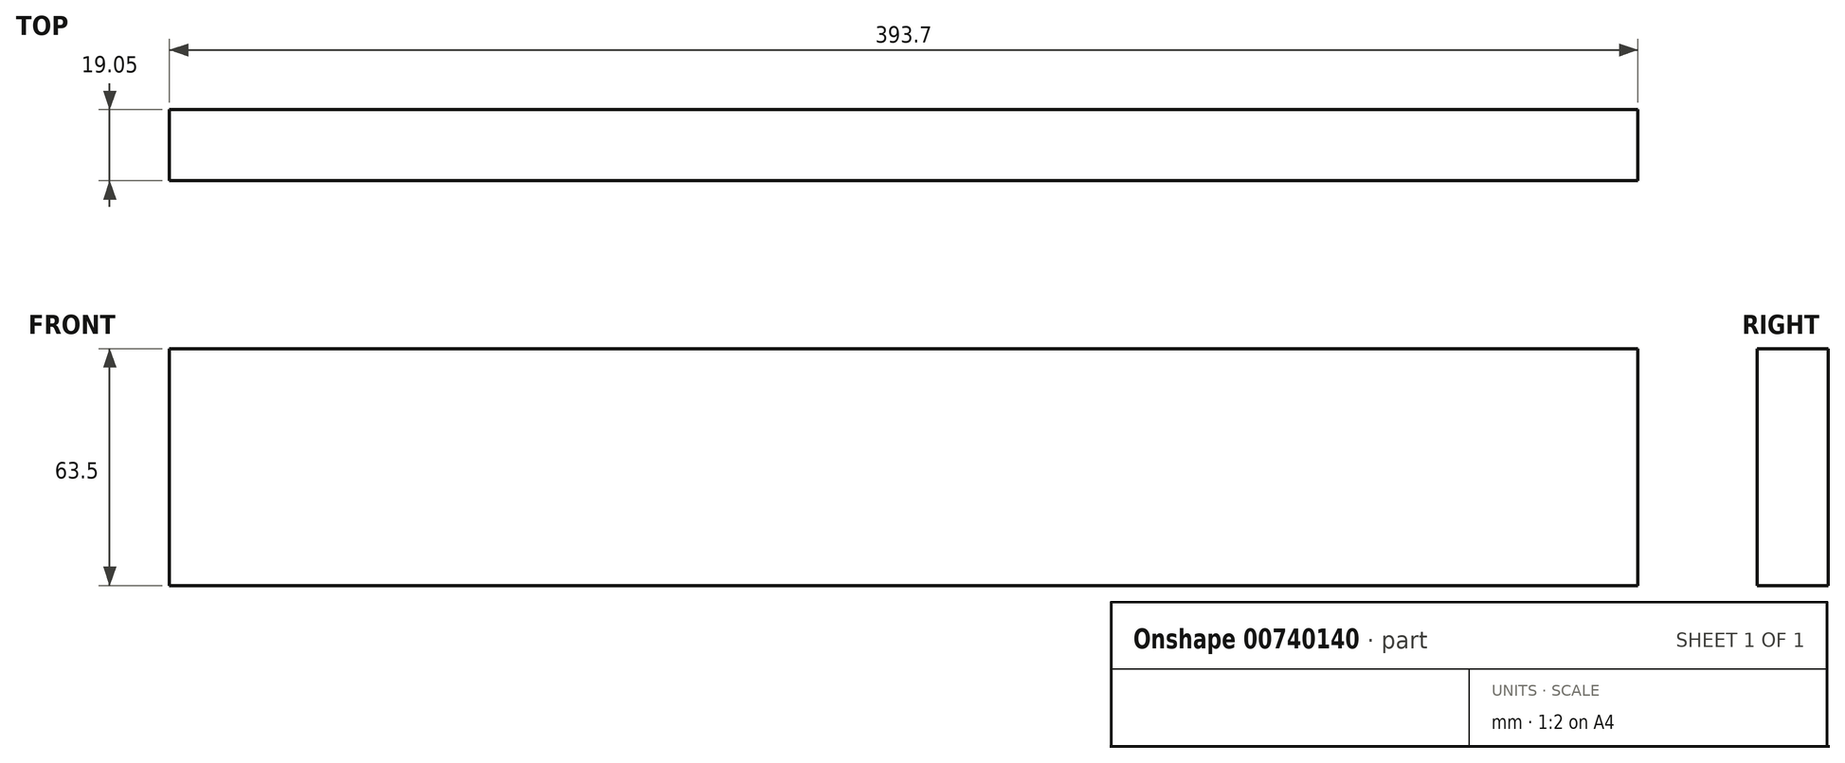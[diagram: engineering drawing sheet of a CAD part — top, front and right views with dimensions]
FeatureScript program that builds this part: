
annotation { "Feature Type Name" : "Feature", "Feature Type Description" : "" }
export const myFeature = defineFeature(function(context is Context, id is Id, definition is map)
    precondition{}
    {
        {
            var Q0;
            Q0=qCreatedBy(makeId("Right.planeOp"),FACE);
            var sketch = newSketch(context, id + "F0", { "sketchPlane" : qUnion([Q0])});
            skLineSegment(sketch, "E0.bottom", {"start": v(-79.68, 59.96) * mm, "end": v(-60.63, 59.96) * mm});
            skLineSegment(sketch, "E0.top", {"start": v(-79.68, -3.54) * mm, "end": v(-60.63, -3.54) * mm});
            skLineSegment(sketch, "E0.left", {"start": v(-79.68, 59.96) * mm, "end": v(-79.68, -3.54) * mm});
            skLineSegment(sketch, "E0.right", {"start": v(-60.63, 59.96) * mm, "end": v(-60.63, -3.54) * mm});
            skSolve(sketch);
        }
        {
            var Q0;
            Q0=makeQuery(id+"F0.imprint","IMPRINT",FACE,{"disambiguationData":[TD([[makeQuery(id+"F0.imprint","IMPRINT",EDGE,{"derivedFrom":sQuery(id+"F0.wireOp",EDGE,"E0.bottom")}),-1.0]])]});
            extrude(context, id + "F1", {"entities" : qUnion([Q0]), "depth" : 393.7 * mm, "offsetDistance" : 25.4 * mm});
        }
    });
